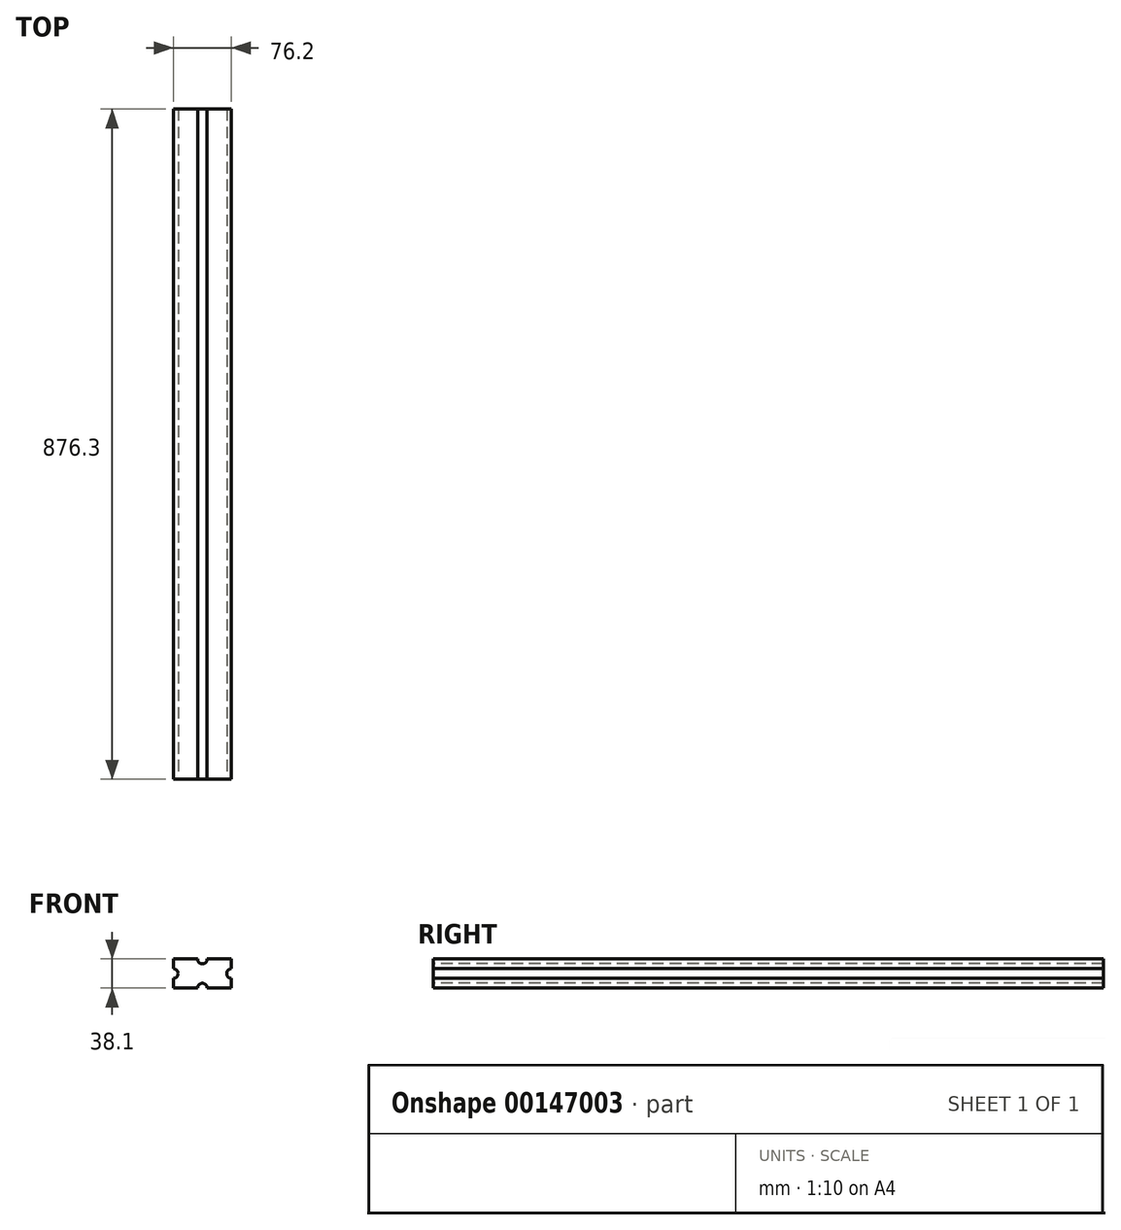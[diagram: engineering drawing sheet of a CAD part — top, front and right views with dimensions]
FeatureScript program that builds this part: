
annotation { "Feature Type Name" : "Feature", "Feature Type Description" : "" }
export const myFeature = defineFeature(function(context is Context, id is Id, definition is map)
    precondition{}
    {
        {
            var Q0;
            Q0=qCreatedBy(makeId("Front.planeOp"),FACE);
            var sketch = newSketch(context, id + "F0", { "sketchPlane" : qUnion([Q0])});
            skLineSegment(sketch, "E0.bottom", {"start": v(-108.5, 64.04) * mm, "end": v(-32.3, 64.04) * mm});
            skLineSegment(sketch, "E0.top", {"start": v(-108.5, 25.94) * mm, "end": v(-32.3, 25.94) * mm});
            skLineSegment(sketch, "E0.left", {"start": v(-108.5, 64.04) * mm, "end": v(-108.5, 25.94) * mm});
            skLineSegment(sketch, "E0.right", {"start": v(-32.3, 64.04) * mm, "end": v(-32.3, 25.94) * mm});
            skSolve(sketch);
        }
        {
            var Q0;
            Q0=makeQuery(id+"F0.imprint","IMPRINT",FACE,{"disambiguationData":[TD([[makeQuery(id+"F0.imprint","IMPRINT",EDGE,{"derivedFrom":sQuery(id+"F0.wireOp",EDGE,"E0.bottom")}),-1.0]])]});
            extrude(context, id + "F1", {"entities" : qUnion([Q0]), "depth" : 876.3 * mm});
        }
        {
            var Q0;
            Q0=makeQuery(id+"F1.opExtrude","CAP_FACE",FACE,{"disambiguationData":[OSD([sQuery(id+"F0.wireOp",EDGE,"E0.bottom"),sQuery(id+"F0.wireOp",EDGE,"E0.top"),sQuery(id+"F0.wireOp",EDGE,"E0.left"),sQuery(id+"F0.wireOp",EDGE,"E0.right")])],"isStart":false});
            var sketch = newSketch(context, id + "F2", { "sketchPlane" : qUnion([Q0])});
            skCircle(sketch, "E1", {"center": v(-70.4, 64.04) * mm, "radius": 6.35 * mm});
            skSolve(sketch);
        }
        {
            var Q0;
            Q0 = qSketchRegion(id + "F2", true);
            extrude(context, id + "F3", {"entities" : qUnion([Q0]), "operationType" : NewBodyOperationType.REMOVE, "oppositeDirection" : true, "depth" : 876.3 * mm});
        }
        {
            var Q0;
            Q0=makeQuery(id+"F1.opExtrude","CAP_FACE",FACE,{"disambiguationData":[OSD([sQuery(id+"F0.wireOp",EDGE,"E0.bottom"),sQuery(id+"F0.wireOp",EDGE,"E0.top"),sQuery(id+"F0.wireOp",EDGE,"E0.left"),sQuery(id+"F0.wireOp",EDGE,"E0.right")])],"isStart":false});
            var sketch = newSketch(context, id + "F4", { "sketchPlane" : qUnion([Q0])});
            skCircle(sketch, "E2", {"center": v(-32.3, 44.99) * mm, "radius": 6.35 * mm});
            skCircle(sketch, "E3", {"center": v(-108.5, 44.99) * mm, "radius": 6.35 * mm});
            skCircle(sketch, "E4", {"center": v(-70.4, 25.94) * mm, "radius": 6.35 * mm});
            skSolve(sketch);
        }
        {
            var Q0;
            Q0 = qSketchRegion(id + "F4", true);
            extrude(context, id + "F5", {"entities" : qUnion([Q0]), "operationType" : NewBodyOperationType.REMOVE, "oppositeDirection" : true, "depth" : 876.3 * mm});
        }
    });
